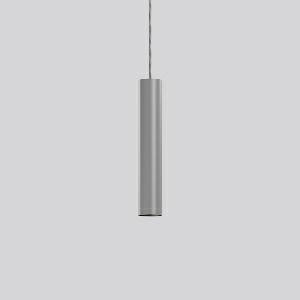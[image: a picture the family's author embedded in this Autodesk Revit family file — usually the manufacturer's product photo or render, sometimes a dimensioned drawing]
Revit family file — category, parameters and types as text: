
# Revit family: deecos_p_micro_911492_004_2_6f59
name_source: partatom
category: Lighting Fixtures
units: mm (PartAtom-declared; Revit-internal decimal feet)

## family parameters
Cut with Voids When Loaded = No
Host = Face
Light Source = No
Part Type = Normal
Room Calculation Point = No
Round Connector Dimension = Use Diameter
Shared = No

## types (1)
- DEECOS P micro (1 x LED Modul 940, 1350 lm, 4000)
    Apparent Load = 16 VA
    CIE Flux Codes = 92 99 100 100 100
    Color Rendering = 92
    Color Temperature = 4000
    Default Elevation = 1800 mm
    Description = Series: DEECOS P micro
Cylindrical pendant luminaire. Housing: die-cast aluminium, powder-coated. Canopy made of powder-coated sheet steel with magnetic attachment. Optical assembly with lens made of plastic (polycarbonate) for the best homogeneous light distribution - can be changed without tools. Black plastic ring and recessed LED to prevent glare from the side. Best colour rendering index Ra>90. Transparent suspension cable 3 m, can be shortened. High quality converter without flickering and stroboscopic effect. 
Colour: silver
Diameter: 60 mm
Height: 340 mm
Suspension length: 3000 mm
Lamp: LED
Socket: without socket
Colour temperature: 4000K
Colour rendering index (CRI): 92
System power: 16 W
Rated luminous flux: 1350 lm
Luminous efficiency: 84 lm/W
Control gear: Regulated power supply
Protection class: I
Type of protection: IP 20
    Height = 340 mm
    Lamp = 1 x LED Modul 940
    Lamp Light Flux = 1350 lm
    Lamp count = 1
    Length = 60 mm  [stored 0.19685 ft]
    Lifetime = 50000 h
    Luminous efficacy = 84 lm/W
    Manufacturer = RZB
    ModVariant = No
    Model = 911492.004.2
    Mounting Place = Ceiling
    Mounting Type = Pendant
    Number of Poles = 1
    OnlyDefault = Yes
    Power Factor = 1
    Product Name = DEECOS P micro
    Product group = Pendant luminaires
    ProductGroupID = 902
    Protection Class = Protection class I
    Protection Degree = Degree of protection
    RLX_Detail_Level = 1
    RLX_Emergency_Light_Flux = 0 lm
    RLX_Emergency_Type = 0
    RLX_Emergency_Type_DB = No
    RlxData = <blob elided: 31257 chars, md5=5661365a>
    Socket = socket
    Standby Power = 0 W
    System Light Flux = 1350 lm
    System Power = 16 W
    Type Comments = Product without accessories
    Type Image = 911491.004.jpg
    URL = http://relux.com
    VarID = ---
    Voltage = 0 V
    Weight = 0.00 kg
    Width = 0 mm  [stored 0 ft]

note: [stored X ft] marks values corroborated as IEEE doubles in the binary element streams (Revit-internal decimal feet)

## geometry (parser evidence)
native form markers: Blend x4, Sweep x10
no freeform markers — native parametric forms only
